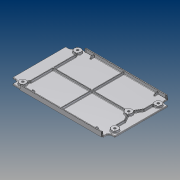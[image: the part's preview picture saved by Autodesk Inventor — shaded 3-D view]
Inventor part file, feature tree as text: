
AUTODESK INVENTOR PART (.ipt)
format: ipt  version: 2012 (Build 160160000, 160)  size: 1,644,544 bytes
history: native  units: mm (DEFAULTED — no unit token found)
features: sketch x7, fillet x7, extrude x6, other x4, plane x3, hole x1, draft x1, pattern_linear x1
ambient origin geometry x5: Origin, X Axis, Y Axis, Z Axis, Center Point
bodies: Solid1 (feature_tree)
feature tree (30):
  sketch  "Sketch2"  dims[d0=0.79375mm d1=209.55mm]
  extrude  "Extrusion1"  Depth=209.55mm
  extrude  "Extrusion3"  Depth=223.393mm
  hole  "Hole1"  [1 undecoded]
  draft  "FaceDraft1"
  extrude  "Side Wings"  Depth=4.4704mm TaperAngle=0.0deg
  other  "Side Wing End Draft"
  other  "Side Wing Inside Draft"
  other  "Ribs"
  extrude  "Rib Shaping"  Depth=2.54mm
  pattern_linear  "Rib Shaping Pattern"  Count1=12  [1 undecoded]
  extrude  "Side Wing Tips"  TaperAngle=0.0deg  [1 undecoded]
  other  "Side Wing Tips Draft"
  extrude  "Velcro Cut"  Depth=17.272mm
  fillet  "Rib Joining Fillets"  Radius=40.0mm
  fillet  "Fillet5"  Radius=55.0mm
  fillet  "Fillet6"  Radius=10.0mm
  fillet  "Top Fillets"  Radius=44.5mm
  fillet  "Bottom Fillets"  Radius=172.0mm
  fillet  "Velcro Corner Fillet"  Radius=0.349066mm
  fillet  "Velcro Edge Fillet"  Radius=0.79375mm
  plane  "YZ Plane (RIGHT)"
  plane  "XZ Plane (TOP)"
  plane  "XY Plane (FRONT)"
  sketch  "Sketch4"  dims[d2=127.0mm d4=223.393mm]
  sketch  "Sketch5"  dims[d5=140.843mm d6=2.54mm d7=0.349066mm]
  sketch  "Sketch6"  dims[d13=5.5626mm d14=4.4704mm d15=0.0mm]
  sketch  "Sketch7"  dims[d16=5.4864mm d17=12.7mm d18=10.6172mm d19=4.4704mm d20=14.3117mm d21=19.05mm d22=20.594885mm d23=2.54mm]
  sketch  "Sketch8"  dims[d25=17.0mm]
  sketch  "Sketch9"  dims[d26=95.0mm d27=120.0mm d28=0.0mm d29=17.272mm d30=40.0mm d31=55.0mm d32=10.0mm d33=44.5mm d34=172.0mm d35=0.349066mm d36=0.79375mm d37=1.27mm d38=1.27mm d39=1.27mm d40=0.396875mm d41=0.79375mm d42=26.67mm d43=101.6mm d44=1.27mm d46=1.27mm d47=-7.853982mm d48=3.175mm d49=1.5875mm d50=143.8656mm d51=3.048mm d52=9.398mm d53=-0.523599mm d54=-0.698132mm d55=96.8502mm d56=82.3722mm d57=98.4504mm d58=80.6704mm d59=0.396875mm d61=1.778mm d62=2.54mm d63=0.349066mm d64=139.7mm d66=123.19mm d67=0.174533mm d68=45.0deg d69=1.5875mm d70=1.5875mm d71=25.4mm d72=0.0mm d73=139.7mm d74=139.7mm d75=25.4mm d76=0.349066mm d78=1.27mm d79=0.359413mm d80=0.174533mm d85=0.359413mm d86=30.0deg d87=1.27mm d88=0.508mm d90=1.27mm d91=1.27mm d92=0.508mm d93=1.27mm d94=1.27mm d95=0.79375mm d97=0.396875mm d100=0.79375mm d105=0.254mm d110=26.543mm d111=91.2mm d112=166.243mm d113=6.35mm d114=60.0deg d115=184.15mm d116=20.0mm d118=139.7mm d119=1.016mm d120=3.048mm d121=60.325mm]
note: 3 required parameter values undecoded (feature->parameter linkage not recoverable at this tier; creation-order binding heuristic only, values carry confidence <= 0.55)
